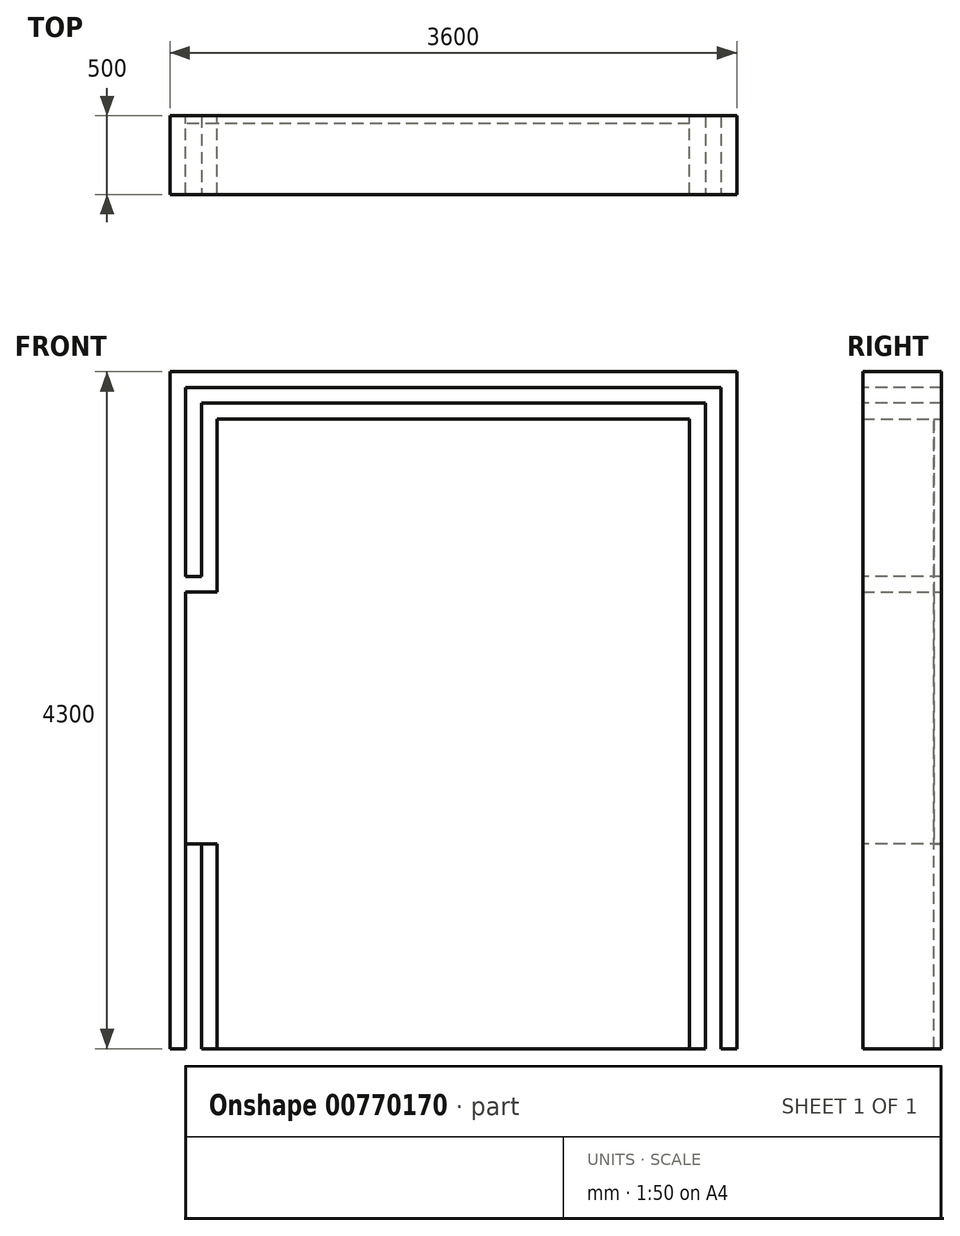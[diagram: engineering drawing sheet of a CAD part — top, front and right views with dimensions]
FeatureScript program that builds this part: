
annotation { "Feature Type Name" : "Feature", "Feature Type Description" : "" }
export const myFeature = defineFeature(function(context is Context, id is Id, definition is map)
    precondition{}
    {
        {
            var Q0;
            Q0=qCreatedBy(makeId("Front.planeOp"),FACE);
            var sketch = newSketch(context, id + "F0", { "sketchPlane" : qUnion([Q0])});
            skLineSegment(sketch, "E0", {"start": v(-1826.58, 0) * mm, "end": v(-1826.58, 4300) * mm});
            skLineSegment(sketch, "E1", {"start": v(-1826.58, 4300) * mm, "end": v(1773.42, 4300) * mm});
            skLineSegment(sketch, "E2", {"start": v(1773.42, 4300) * mm, "end": v(1773.42, 0) * mm});
            skLineSegment(sketch, "E3", {"start": v(1773.42, 0) * mm, "end": v(1473.42, 0) * mm});
            skLineSegment(sketch, "E4", {"start": v(1473.42, 0) * mm, "end": v(1473.42, 4000) * mm});
            skLineSegment(sketch, "E5", {"start": v(1473.42, 4000) * mm, "end": v(-1526.58, 4000) * mm});
            skLineSegment(sketch, "E6", {"start": v(-1526.58, 4000) * mm, "end": v(-1526.58, 2900) * mm});
            skLineSegment(sketch, "E7", {"start": v(-1526.58, 2900) * mm, "end": v(-1726.58, 2900) * mm});
            skLineSegment(sketch, "E8", {"start": v(-1726.58, 2900) * mm, "end": v(-1726.58, 1300) * mm});
            skLineSegment(sketch, "E9", {"start": v(-1726.58, 1300) * mm, "end": v(-1526.58, 1300) * mm});
            skLineSegment(sketch, "E10", {"start": v(-1526.58, 1300) * mm, "end": v(-1526.58, 0) * mm});
            skLineSegment(sketch, "E11", {"start": v(-1526.58, 0) * mm, "end": v(-1826.58, 0) * mm});
            skSolve(sketch);
        }
        {
            var Q0;
            Q0 = qSketchRegion(id + "F0", true);
            extrude(context, id + "F1", {"entities" : qUnion([Q0]), "depth" : 500 * mm, "offsetDistance" : 25 * mm});
        }
        {
            var Q0;
            Q0=makeQuery(id+"F1.opExtrude","CAP_FACE",FACE,{"disambiguationData":[OSD([sQuery(id+"F0.wireOp",EDGE,"E0"),sQuery(id+"F0.wireOp",EDGE,"E1"),sQuery(id+"F0.wireOp",EDGE,"E2"),sQuery(id+"F0.wireOp",EDGE,"E3"),sQuery(id+"F0.wireOp",EDGE,"E4"),sQuery(id+"F0.wireOp",EDGE,"E5"),sQuery(id+"F0.wireOp",EDGE,"E6"),sQuery(id+"F0.wireOp",EDGE,"E7"),sQuery(id+"F0.wireOp",EDGE,"E8"),sQuery(id+"F0.wireOp",EDGE,"E9"),sQuery(id+"F0.wireOp",EDGE,"E10"),sQuery(id+"F0.wireOp",EDGE,"E11")])],"isStart":false});
            var sketch = newSketch(context, id + "F2", { "sketchPlane" : qUnion([Q0])});
            skLineSegment(sketch, "E12", {"start": v(-1726.58, 3000) * mm, "end": v(-1726.58, 4200) * mm});
            skLineSegment(sketch, "E13", {"start": v(-1726.58, 4200) * mm, "end": v(1673.42, 4200) * mm});
            skLineSegment(sketch, "E14", {"start": v(1673.42, 4200) * mm, "end": v(1673.42, 0) * mm});
            skLineSegment(sketch, "E15", {"start": v(1673.42, 0) * mm, "end": v(1573.42, 0) * mm});
            skLineSegment(sketch, "E16", {"start": v(1573.42, 0) * mm, "end": v(1573.42, 4100) * mm});
            skLineSegment(sketch, "E17", {"start": v(1573.42, 4100) * mm, "end": v(-1626.58, 4100) * mm});
            skLineSegment(sketch, "E18", {"start": v(-1626.58, 4100) * mm, "end": v(-1626.58, 3000) * mm});
            skLineSegment(sketch, "E19", {"start": v(-1626.58, 3000) * mm, "end": v(-1726.58, 3000) * mm});
            skLineSegment(sketch, "E20.bottom", {"start": v(-1726.58, 1300) * mm, "end": v(-1626.58, 1300) * mm});
            skLineSegment(sketch, "E20.top", {"start": v(-1726.58, 0) * mm, "end": v(-1626.58, 0) * mm});
            skLineSegment(sketch, "E20.left", {"start": v(-1726.58, 1300) * mm, "end": v(-1726.58, 0) * mm});
            skLineSegment(sketch, "E20.right", {"start": v(-1626.58, 1300) * mm, "end": v(-1626.58, 0) * mm});
            skSolve(sketch);
        }
        {
            var Q0;
            Q0 = qSketchRegion(id + "F2", true);
            extrude(context, id + "F3", {"entities" : qUnion([Q0]), "operationType" : NewBodyOperationType.REMOVE, "endBound" : BoundingType.THROUGH_ALL, "oppositeDirection" : true, "depth" : 25 * mm, "offsetDistance" : 25 * mm});
        }
        {
            var Q0;
            {var subQ0=sQuery(id+"F0.wireOp",EDGE,"E11");var subQ1=sQuery(id+"F0.wireOp",EDGE,"E8");var subQ2=sQuery(id+"F0.wireOp",EDGE,"E7");var subQ3=sQuery(id+"F0.wireOp",EDGE,"E6");var subQ4=sQuery(id+"F0.wireOp",EDGE,"E5");var subQ5=sQuery(id+"F0.wireOp",EDGE,"E4");var subQ6=sQuery(id+"F0.wireOp",EDGE,"E0");var subQ7=sQuery(id+"F0.wireOp",EDGE,"E3");var subQ8=sQuery(id+"F0.wireOp",EDGE,"E1");var subQ9=sQuery(id+"F0.wireOp",EDGE,"E2");Q0=makeQuery(id+"F3.boolean.opBoolean","SPLIT",FACE,{"disambiguationData":[TD([makeQuery(id+"F1.opExtrude","SWEPT_FACE",FACE,{"disambiguationData":[OSD([subQ6])]})])],"derivedFrom":makeQuery(id+"F1.opExtrude","CAP_FACE",FACE,{"disambiguationData":[OSD([subQ6,subQ8,subQ9,subQ7,subQ5,subQ4,subQ3,subQ2,subQ1,sQuery(id+"F0.wireOp",EDGE,"E9"),sQuery(id+"F0.wireOp",EDGE,"E10"),subQ0])],"isStart":true})});}
            var sketch = newSketch(context, id + "F4", { "sketchPlane" : qUnion([Q0])});
            skLineSegment(sketch, "E21", {"start": v(1526.97, 0) * mm, "end": v(1526.97, 1299.64) * mm});
            skLineSegment(sketch, "E22", {"start": v(1526.97, 1299.64) * mm, "end": v(1726.58, 1299.64) * mm});
            skLineSegment(sketch, "E23", {"start": v(1726.58, 1299.64) * mm, "end": v(1726.58, 2900) * mm});
            skLineSegment(sketch, "E24", {"start": v(1726.58, 2900) * mm, "end": v(1526.58, 2900) * mm});
            skLineSegment(sketch, "E25", {"start": v(1526.58, 2900) * mm, "end": v(1526.58, 4000) * mm});
            skLineSegment(sketch, "E26", {"start": v(1526.58, 4000) * mm, "end": v(-1473.42, 4000) * mm});
            skLineSegment(sketch, "E27", {"start": v(-1473.42, 4000) * mm, "end": v(-1473.42, 0) * mm});
            skLineSegment(sketch, "E28", {"start": v(-1473.42, 0) * mm, "end": v(1526.97, 0) * mm});
            skSolve(sketch);
        }
        {
            var Q0;
            Q0 = qSketchRegion(id + "F4", true);
            extrude(context, id + "F5", {"entities" : qUnion([Q0]), "oppositeDirection" : true, "depth" : 50 * mm, "offsetDistance" : 25 * mm});
        }
    });
